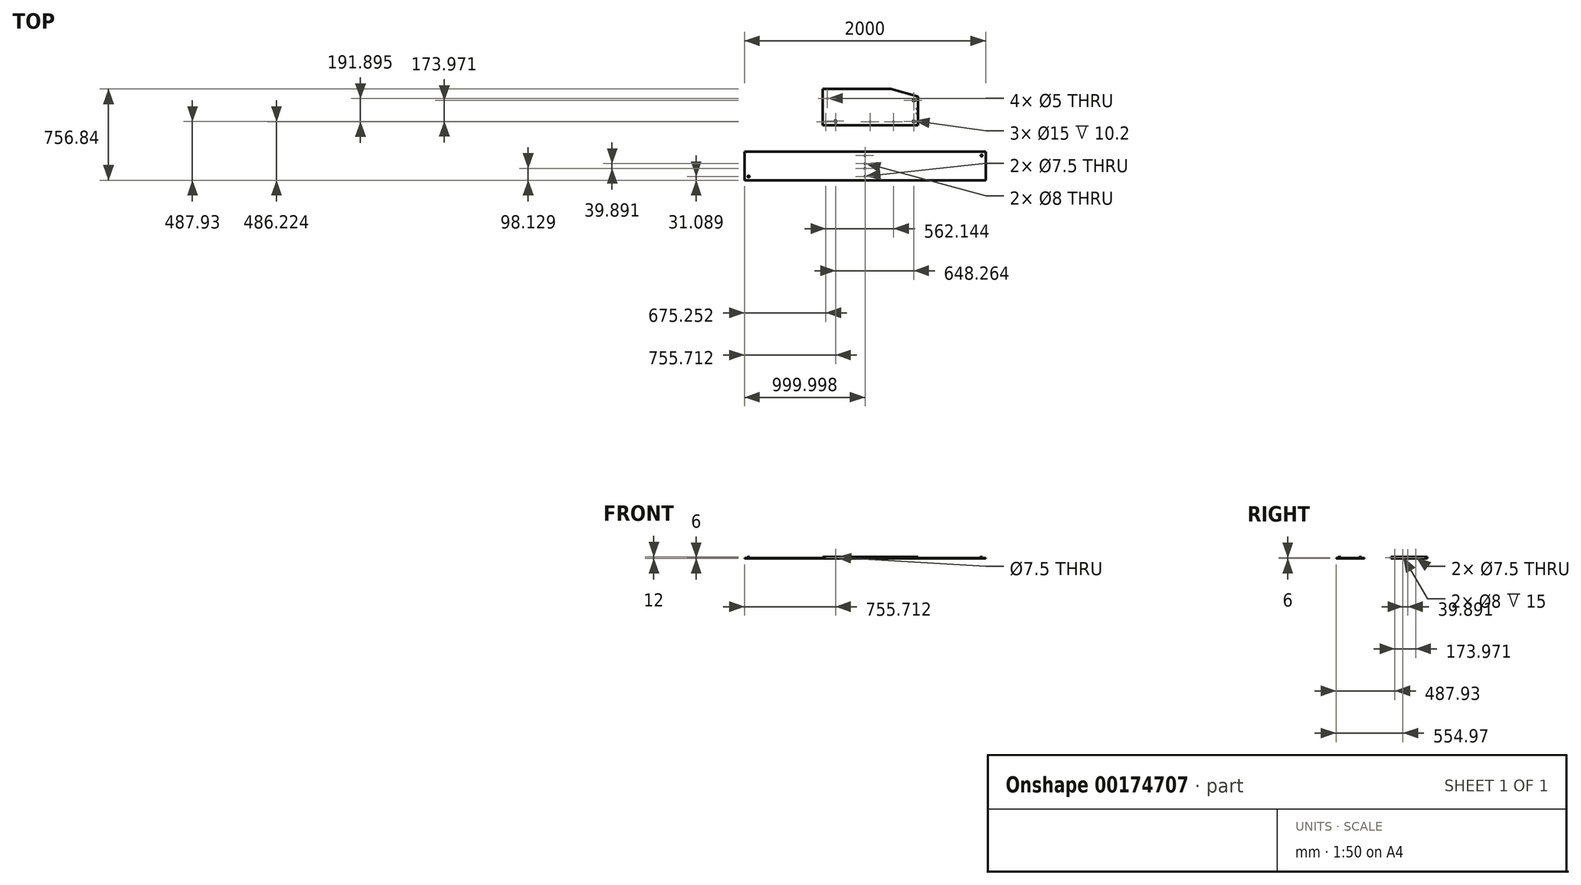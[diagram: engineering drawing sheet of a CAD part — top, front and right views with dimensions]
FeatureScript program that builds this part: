
annotation { "Feature Type Name" : "Feature", "Feature Type Description" : "" }
export const myFeature = defineFeature(function(context is Context, id is Id, definition is map)
    precondition{}
    {
        {
            var Q0;
            Q0=qCreatedBy(makeId("Top.planeOp"),FACE);
            var sketch = newSketch(context, id + "F0", { "sketchPlane" : qUnion([Q0])});
            skLineSegment(sketch, "E0.bottom", {"start": v(72.05, 333.85) * mm, "end": v(72.05, 33.85) * mm});
            skLineSegment(sketch, "E0.top", {"start": v(862.05, 270) * mm, "end": v(862.05, 33.85) * mm});
            skLineSegment(sketch, "E0.left", {"start": v(72.05, 333.85) * mm, "end": v(637.18, 333.85) * mm});
            skLineSegment(sketch, "E0.right", {"start": v(72.05, 33.85) * mm, "end": v(862.05, 33.85) * mm});
            skLineSegment(sketch, "E1", {"start": v(862.05, 270) * mm, "end": v(637.18, 333.85) * mm});
            skLineSegment(sketch, "E2.bottom", {"start": v(-575.93, -186.84) * mm, "end": v(1424.07, -186.84) * mm});
            skLineSegment(sketch, "E2.top", {"start": v(-575.93, -423) * mm, "end": v(1424.07, -423) * mm});
            skLineSegment(sketch, "E2.left", {"start": v(-575.93, -186.84) * mm, "end": v(-575.93, -423) * mm});
            skLineSegment(sketch, "E2.right", {"start": v(1424.07, -186.84) * mm, "end": v(1424.07, -423) * mm});
            skSolve(sketch);
        }
        {
            var Q0;
            Q0=makeQuery(id+"F0.imprint","IMPRINT",FACE,{"disambiguationData":[TD([[makeQuery(id+"F0.imprint","IMPRINT",EDGE,{"derivedFrom":sQuery(id+"F0.wireOp",EDGE,"E0.bottom")}),1.0]])]});
            var Q1;
            Q1=makeQuery(id+"F0.imprint","IMPRINT",FACE,{"disambiguationData":[TD([[makeQuery(id+"F0.imprint","IMPRINT",EDGE,{"derivedFrom":sQuery(id+"F0.wireOp",EDGE,"E2.bottom")}),-1.0]])]});
            extrude(context, id + "F1", {"entities" : qUnion([Q0, Q1]), "oppositeDirection" : true, "depth" : 12 * mm});
        }
        {
            var Q0;
            Q0=makeQuery(id+"F1.opExtrude","CAP_FACE",FACE,{"disambiguationData":[OSD([sQuery(id+"F0.wireOp",EDGE,"E0.bottom"),sQuery(id+"F0.wireOp",EDGE,"E0.top"),sQuery(id+"F0.wireOp",EDGE,"E0.left"),sQuery(id+"F0.wireOp",EDGE,"E0.right"),sQuery(id+"F0.wireOp",EDGE,"E1")])],"isStart":true});
            var sketch = newSketch(context, id + "F2", { "sketchPlane" : qUnion([Q0])});
            skCircle(sketch, "E3", {"center": v(828.05, 238.91) * mm, "radius": 7.5 * mm});
            skCircle(sketch, "E4", {"center": v(828.05, 64.94) * mm, "radius": 7.5 * mm});
            skCircle(sketch, "E5", {"center": v(661.47, 63.23) * mm, "radius": 2.5 * mm});
            skCircle(sketch, "E6", {"center": v(467.05, 63.23) * mm, "radius": 2.5 * mm});
            skCircle(sketch, "E7", {"center": v(99.32, 63.23) * mm, "radius": 2.5 * mm});
            skCircle(sketch, "E8", {"center": v(179.78, 67.85) * mm, "radius": 7.5 * mm});
            skCircle(sketch, "E9", {"center": v(112.37, 255.13) * mm, "radius": 2.5 * mm});
            skLineSegment(sketch, "E10", {"start": v(179.78, 67.85) * mm, "end": v(179.78, 33.85) * mm, "construction": true});
            skLineSegment(sketch, "E11", {"start": v(828.05, 64.94) * mm, "end": v(862.05, 64.94) * mm, "construction": true});
            skLineSegment(sketch, "E12", {"start": v(828.05, 238.91) * mm, "end": v(862.05, 238.91) * mm, "construction": true});
            skLineSegment(sketch, "E13", {"start": v(112.37, 255.13) * mm, "end": v(72.05, 255.13) * mm, "construction": true});
            skLineSegment(sketch, "E14", {"start": v(99.32, 63.23) * mm, "end": v(99.32, 33.85) * mm, "construction": true});
            skLineSegment(sketch, "E15", {"start": v(467.05, 63.23) * mm, "end": v(467.05, 33.85) * mm, "construction": true});
            skLineSegment(sketch, "E16", {"start": v(661.47, 63.23) * mm, "end": v(661.47, 33.85) * mm, "construction": true});
            skLineSegment(sketch, "E17", {"start": v(862.05, 151.93) * mm, "end": v(72.05, 151.93) * mm, "construction": true});
            skPoint(sketch, "E17.endSnap0", {"position": v(862.05, 151.93) * mm});
            skSolve(sketch);
        }
        {
            var Q0;
            Q0=makeQuery(id+"F1.opExtrude","SWEPT_FACE",FACE,{"disambiguationData":[OSD([sQuery(id+"F0.wireOp",EDGE,"E0.top")])]});
            var sketch = newSketch(context, id + "F3", { "sketchPlane" : qUnion([Q0])});
            skLineSegment(sketch, "E18", {"start": v(64.94, 0) * mm, "end": v(64.94, -12) * mm, "construction": true});
            skLineSegment(sketch, "E19", {"start": v(238.91, 0) * mm, "end": v(238.91, -12) * mm, "construction": true});
            skCircle(sketch, "E20", {"center": v(64.94, -6) * mm, "radius": 3.75 * mm});
            skCircle(sketch, "E21", {"center": v(238.91, -6) * mm, "radius": 3.75 * mm});
            skLineSegment(sketch, "E22", {"start": v(131.98, 0) * mm, "end": v(131.98, -12) * mm, "construction": true});
            skLineSegment(sketch, "E23", {"start": v(171.87, 0) * mm, "end": v(171.87, -12) * mm, "construction": true});
            skCircle(sketch, "E24", {"center": v(131.98, -6) * mm, "radius": 4 * mm});
            skCircle(sketch, "E25", {"center": v(171.87, -6) * mm, "radius": 4 * mm});
            skLineSegment(sketch, "E26", {"start": v(151.93, -12) * mm, "end": v(151.93, 0) * mm, "construction": true});
            skLineSegment(sketch, "E27", {"start": v(238.91, -6) * mm, "end": v(64.94, -6) * mm, "construction": true});
            skLineSegment(sketch, "E28", {"start": v(171.87, -6) * mm, "end": v(131.98, -6) * mm, "construction": true});
            skSolve(sketch);
        }
        {
            var Q0;
            Q0=makeQuery(id+"F1.opExtrude","SWEPT_FACE",FACE,{"disambiguationData":[OSD([sQuery(id+"F0.wireOp",EDGE,"E0.right")])]});
            var sketch = newSketch(context, id + "F4", { "sketchPlane" : qUnion([Q0])});
            skLineSegment(sketch, "E29", {"start": v(179.78, 0) * mm, "end": v(179.78, -12) * mm, "construction": true});
            skCircle(sketch, "E30", {"center": v(179.78, -6) * mm, "radius": 3.75 * mm});
            skSolve(sketch);
        }
        {
            var Q0;
            Q0=makeQuery(id+"F1.opExtrude","CAP_FACE",FACE,{"disambiguationData":[OSD([sQuery(id+"F0.wireOp",EDGE,"E2.bottom"),sQuery(id+"F0.wireOp",EDGE,"E2.top"),sQuery(id+"F0.wireOp",EDGE,"E2.left"),sQuery(id+"F0.wireOp",EDGE,"E2.right")])],"isStart":true});
            var sketch = newSketch(context, id + "F5", { "sketchPlane" : qUnion([Q0])});
            skLineSegment(sketch, "E31", {"start": v(424.07, -186.84) * mm, "end": v(424.07, -423) * mm, "construction": true});
            skCircle(sketch, "E32", {"center": v(424.07, -217.93) * mm, "radius": 3.75 * mm});
            skCircle(sketch, "E33", {"center": v(424.07, -391.9) * mm, "radius": 3.75 * mm});
            skCircle(sketch, "E34", {"center": v(424.07, -284.97) * mm, "radius": 4 * mm});
            skCircle(sketch, "E35", {"center": v(424.07, -324.86) * mm, "radius": 4 * mm});
            skLineSegment(sketch, "E36", {"start": v(-575.93, -304.92) * mm, "end": v(1424.07, -304.92) * mm, "construction": true});
            skPoint(sketch, "E37", {"position": v(424.07, -304.92) * mm});
            skLineSegment(sketch, "E38", {"start": v(424.07, -391.9) * mm, "end": v(424.07, -217.93) * mm, "construction": true});
            skLineSegment(sketch, "E39", {"start": v(424.07, -324.86) * mm, "end": v(424.07, -284.97) * mm, "construction": true});
            skCircle(sketch, "E40", {"center": v(-541.93, -217.93) * mm, "radius": 7.5 * mm});
            skLineSegment(sketch, "E41", {"start": v(-541.93, -217.93) * mm, "end": v(-575.93, -217.93) * mm, "construction": true});
            skCircle(sketch, "E42.MirrorC", {"center": v(-541.93, -391.9) * mm, "radius": 7.5 * mm});
            skLineSegment(sketch, "E43.MirrorCS", {"start": v(-541.93, -391.9) * mm, "end": v(-575.93, -391.9) * mm, "construction": true});
            skCircle(sketch, "E44.MirrorC", {"center": v(1390.07, -217.93) * mm, "radius": 7.5 * mm});
            skLineSegment(sketch, "E45.MirrorCS", {"start": v(1390.07, -217.93) * mm, "end": v(1424.07, -217.93) * mm, "construction": true});
            skCircle(sketch, "E46.MirrorC", {"center": v(1390.07, -391.9) * mm, "radius": 7.5 * mm});
            skLineSegment(sketch, "E47.MirrorCS", {"start": v(1390.07, -391.9) * mm, "end": v(1424.07, -391.9) * mm, "construction": true});
            skSolve(sketch);
        }
        {
            var Q0;
            Q0=makeQuery(id+"F1.opExtrude","SWEPT_FACE",FACE,{"disambiguationData":[OSD([sQuery(id+"F0.wireOp",EDGE,"E2.right")])]});
            var sketch = newSketch(context, id + "F6", { "sketchPlane" : qUnion([Q0])});
            skLineSegment(sketch, "E48", {"start": v(-391.9, 0) * mm, "end": v(-391.9, -12) * mm, "construction": true});
            skLineSegment(sketch, "E49", {"start": v(-217.93, 0) * mm, "end": v(-217.93, -12) * mm, "construction": true});
            skCircle(sketch, "E50", {"center": v(-391.9, -6) * mm, "radius": 3.75 * mm});
            skCircle(sketch, "E51", {"center": v(-217.93, -6) * mm, "radius": 3.75 * mm});
            skLineSegment(sketch, "E52", {"start": v(-324.86, 0) * mm, "end": v(-324.86, -12) * mm, "construction": true});
            skLineSegment(sketch, "E53", {"start": v(-284.97, 0) * mm, "end": v(-284.97, -12) * mm, "construction": true});
            skCircle(sketch, "E54", {"center": v(-324.86, -6) * mm, "radius": 4 * mm});
            skCircle(sketch, "E55", {"center": v(-284.97, -6) * mm, "radius": 4 * mm});
            skLineSegment(sketch, "E56", {"start": v(-304.92, -12) * mm, "end": v(-304.92, 0) * mm, "construction": true});
            skLineSegment(sketch, "E57", {"start": v(-217.93, -6) * mm, "end": v(-391.9, -6) * mm, "construction": true});
            skLineSegment(sketch, "E58", {"start": v(-284.97, -6) * mm, "end": v(-324.86, -6) * mm, "construction": true});
            skSolve(sketch);
        }
        {
            var Q0;
            Q0=makeQuery(id+"F1.opExtrude","SWEPT_FACE",FACE,{"disambiguationData":[OSD([sQuery(id+"F0.wireOp",EDGE,"E2.left")])]});
            var sketch = newSketch(context, id + "F7", { "sketchPlane" : qUnion([Q0])});
            skLineSegment(sketch, "E59", {"start": v(217.93, 0) * mm, "end": v(217.93, -12) * mm, "construction": true});
            skLineSegment(sketch, "E60", {"start": v(391.9, 0) * mm, "end": v(391.9, -12) * mm, "construction": true});
            skCircle(sketch, "E61", {"center": v(217.93, -6) * mm, "radius": 3.75 * mm});
            skCircle(sketch, "E62", {"center": v(391.9, -6) * mm, "radius": 3.75 * mm});
            skLineSegment(sketch, "E63", {"start": v(284.97, 0) * mm, "end": v(284.97, -12) * mm, "construction": true});
            skLineSegment(sketch, "E64", {"start": v(324.86, 0) * mm, "end": v(324.86, -12) * mm, "construction": true});
            skCircle(sketch, "E65", {"center": v(284.97, -6) * mm, "radius": 4 * mm});
            skCircle(sketch, "E66", {"center": v(324.86, -6) * mm, "radius": 4 * mm});
            skLineSegment(sketch, "E67", {"start": v(304.92, -12) * mm, "end": v(304.92, 0) * mm, "construction": true});
            skLineSegment(sketch, "E68", {"start": v(391.9, -6) * mm, "end": v(217.93, -6) * mm, "construction": true});
            skLineSegment(sketch, "E69", {"start": v(324.86, -6) * mm, "end": v(284.97, -6) * mm, "construction": true});
            skSolve(sketch);
        }
        {
            var Q0;
            Q0=makeQuery(id+"F2.imprint","IMPRINT",FACE,{"disambiguationData":[TD([[makeQuery(id+"F2.imprint","IMPRINT",EDGE,{"derivedFrom":sQuery(id+"F2.wireOp",EDGE,"E8")}),1.0]])]});
            var Q1;
            Q1=makeQuery(id+"F2.imprint","IMPRINT",FACE,{"disambiguationData":[TD([[makeQuery(id+"F2.imprint","IMPRINT",EDGE,{"derivedFrom":sQuery(id+"F2.wireOp",EDGE,"E4")}),1.0]])]});
            var Q2;
            Q2=makeQuery(id+"F2.imprint","IMPRINT",FACE,{"disambiguationData":[TD([[makeQuery(id+"F2.imprint","IMPRINT",EDGE,{"derivedFrom":sQuery(id+"F2.wireOp",EDGE,"E3")}),1.0]])]});
            var Q3;
            Q3=makeQuery(id+"F5.imprint","IMPRINT",FACE,{"disambiguationData":[TD([[makeQuery(id+"F5.imprint","IMPRINT",EDGE,{"derivedFrom":sQuery(id+"F5.wireOp",EDGE,"E40")}),1.0]])]});
            var Q4;
            Q4=makeQuery(id+"F5.imprint","IMPRINT",FACE,{"disambiguationData":[TD([[makeQuery(id+"F5.imprint","IMPRINT",EDGE,{"derivedFrom":sQuery(id+"F5.wireOp",EDGE,"E42.MirrorC")}),-1.0]])]});
            var Q5;
            Q5=makeQuery(id+"F5.imprint","IMPRINT",FACE,{"disambiguationData":[TD([[makeQuery(id+"F5.imprint","IMPRINT",EDGE,{"derivedFrom":sQuery(id+"F5.wireOp",EDGE,"E44.MirrorC")}),-1.0]])]});
            var Q6;
            Q6=makeQuery(id+"F5.imprint","IMPRINT",FACE,{"disambiguationData":[TD([[makeQuery(id+"F5.imprint","IMPRINT",EDGE,{"derivedFrom":sQuery(id+"F5.wireOp",EDGE,"E46.MirrorC")}),1.0]])]});
            var Q7;
            Q7=sQuery(id+"F2.wireOp",EDGE,"E8");
            var Q8;
            Q8=sQuery(id+"F2.wireOp",EDGE,"E4");
            var Q9;
            Q9=sQuery(id+"F2.wireOp",EDGE,"E3");
            extrude(context, id + "F8", {"entities" : qUnion([Q0, Q1, Q2, Q3, Q4, Q5, Q6]), "operationType" : NewBodyOperationType.REMOVE, "surfaceEntities" : qUnion([Q7, Q8, Q9]), "oppositeDirection" : true, "depth" : 10.2 * mm});
        }
        {
            var Q0;
            Q0=makeQuery(id+"F3.imprint","IMPRINT",FACE,{"disambiguationData":[TD([[makeQuery(id+"F3.imprint","IMPRINT",EDGE,{"derivedFrom":sQuery(id+"F3.wireOp",EDGE,"E20")}),1.0]])]});
            var Q1;
            Q1=makeQuery(id+"F3.imprint","IMPRINT",FACE,{"disambiguationData":[TD([[makeQuery(id+"F3.imprint","IMPRINT",EDGE,{"derivedFrom":sQuery(id+"F3.wireOp",EDGE,"E21")}),1.0]])]});
            var Q2;
            Q2=makeQuery(id+"F6.imprint","IMPRINT",FACE,{"disambiguationData":[TD([[makeQuery(id+"F6.imprint","IMPRINT",EDGE,{"derivedFrom":sQuery(id+"F6.wireOp",EDGE,"E51")}),1.0]])]});
            var Q3;
            Q3=makeQuery(id+"F6.imprint","IMPRINT",FACE,{"disambiguationData":[TD([[makeQuery(id+"F6.imprint","IMPRINT",EDGE,{"derivedFrom":sQuery(id+"F6.wireOp",EDGE,"E50")}),1.0]])]});
            var Q4;
            Q4=sQuery(id+"F3.wireOp",EDGE,"E20");
            var Q5;
            Q5=sQuery(id+"F3.wireOp",EDGE,"E21");
            extrude(context, id + "F9", {"entities" : qUnion([Q0, Q1, Q2, Q3]), "operationType" : NewBodyOperationType.REMOVE, "surfaceEntities" : qUnion([Q4, Q5]), "endBound" : BoundingType.UP_TO_NEXT, "oppositeDirection" : true, "depth" : 34 * mm});
        }
        {
            var Q0;
            Q0=makeQuery(id+"F4.imprint","IMPRINT",FACE,{"disambiguationData":[TD([[makeQuery(id+"F4.imprint","IMPRINT",EDGE,{"derivedFrom":sQuery(id+"F4.wireOp",EDGE,"E30")}),1.0]])]});
            extrude(context, id + "F10", {"entities" : qUnion([Q0]), "operationType" : NewBodyOperationType.REMOVE, "endBound" : BoundingType.UP_TO_NEXT, "oppositeDirection" : true, "depth" : 25 * mm});
        }
        {
            var Q0;
            Q0=makeQuery(id+"F2.imprint","IMPRINT",FACE,{"disambiguationData":[TD([[makeQuery(id+"F2.imprint","IMPRINT",EDGE,{"derivedFrom":sQuery(id+"F2.wireOp",EDGE,"E9")}),1.0]])]});
            var Q1;
            Q1=makeQuery(id+"F2.imprint","IMPRINT",FACE,{"disambiguationData":[TD([[makeQuery(id+"F2.imprint","IMPRINT",EDGE,{"derivedFrom":sQuery(id+"F2.wireOp",EDGE,"E7")}),1.0]])]});
            var Q2;
            Q2=makeQuery(id+"F2.imprint","IMPRINT",FACE,{"disambiguationData":[TD([[makeQuery(id+"F2.imprint","IMPRINT",EDGE,{"derivedFrom":sQuery(id+"F2.wireOp",EDGE,"E5")}),1.0]])]});
            var Q3;
            Q3=makeQuery(id+"F2.imprint","IMPRINT",FACE,{"disambiguationData":[TD([[makeQuery(id+"F2.imprint","IMPRINT",EDGE,{"derivedFrom":sQuery(id+"F2.wireOp",EDGE,"E6")}),1.0]])]});
            var Q4;
            Q4=makeQuery(id+"F5.imprint","IMPRINT",FACE,{"disambiguationData":[TD([[makeQuery(id+"F5.imprint","IMPRINT",EDGE,{"derivedFrom":sQuery(id+"F5.wireOp",EDGE,"E32")}),1.0]])]});
            var Q5;
            Q5=makeQuery(id+"F5.imprint","IMPRINT",FACE,{"disambiguationData":[TD([[makeQuery(id+"F5.imprint","IMPRINT",EDGE,{"derivedFrom":sQuery(id+"F5.wireOp",EDGE,"E34")}),1.0]])]});
            var Q6;
            Q6=makeQuery(id+"F5.imprint","IMPRINT",FACE,{"disambiguationData":[TD([[makeQuery(id+"F5.imprint","IMPRINT",EDGE,{"derivedFrom":sQuery(id+"F5.wireOp",EDGE,"E35")}),1.0]])]});
            var Q7;
            Q7=makeQuery(id+"F5.imprint","IMPRINT",FACE,{"disambiguationData":[TD([[makeQuery(id+"F5.imprint","IMPRINT",EDGE,{"derivedFrom":sQuery(id+"F5.wireOp",EDGE,"E33")}),1.0]])]});
            extrude(context, id + "F11", {"entities" : qUnion([Q0, Q1, Q2, Q3, Q4, Q5, Q6, Q7]), "operationType" : NewBodyOperationType.REMOVE, "endBound" : BoundingType.THROUGH_ALL, "oppositeDirection" : true, "depth" : 9 * mm});
        }
        {
            var Q0;
            Q0=makeQuery(id+"F3.imprint","IMPRINT",FACE,{"disambiguationData":[TD([[makeQuery(id+"F3.imprint","IMPRINT",EDGE,{"derivedFrom":sQuery(id+"F3.wireOp",EDGE,"E24")}),1.0]])]});
            var Q1;
            Q1=makeQuery(id+"F3.imprint","IMPRINT",FACE,{"disambiguationData":[TD([[makeQuery(id+"F3.imprint","IMPRINT",EDGE,{"derivedFrom":sQuery(id+"F3.wireOp",EDGE,"E25")}),1.0]])]});
            var Q2;
            Q2=makeQuery(id+"F6.imprint","IMPRINT",FACE,{"disambiguationData":[TD([[makeQuery(id+"F6.imprint","IMPRINT",EDGE,{"derivedFrom":sQuery(id+"F6.wireOp",EDGE,"E55")}),1.0]])]});
            var Q3;
            Q3=makeQuery(id+"F6.imprint","IMPRINT",FACE,{"disambiguationData":[TD([[makeQuery(id+"F6.imprint","IMPRINT",EDGE,{"derivedFrom":sQuery(id+"F6.wireOp",EDGE,"E54")}),1.0]])]});
            extrude(context, id + "F12", {"entities" : qUnion([Q0, Q1, Q2, Q3]), "operationType" : NewBodyOperationType.REMOVE, "oppositeDirection" : true, "depth" : 15 * mm});
        }
        {
            var Q0;
            Q0=makeQuery(id+"F7.imprint","IMPRINT",FACE,{"disambiguationData":[TD([[makeQuery(id+"F7.imprint","IMPRINT",EDGE,{"derivedFrom":sQuery(id+"F7.wireOp",EDGE,"E62")}),1.0]])]});
            var Q1;
            Q1=makeQuery(id+"F7.imprint","IMPRINT",FACE,{"disambiguationData":[TD([[makeQuery(id+"F7.imprint","IMPRINT",EDGE,{"derivedFrom":sQuery(id+"F7.wireOp",EDGE,"E61")}),1.0]])]});
            extrude(context, id + "F13", {"entities" : qUnion([Q0, Q1]), "operationType" : NewBodyOperationType.REMOVE, "endBound" : BoundingType.UP_TO_NEXT, "oppositeDirection" : true, "depth" : 25 * mm});
        }
        {
            var Q0;
            Q0=makeQuery(id+"F7.imprint","IMPRINT",FACE,{"disambiguationData":[TD([[makeQuery(id+"F7.imprint","IMPRINT",EDGE,{"derivedFrom":sQuery(id+"F7.wireOp",EDGE,"E65")}),1.0]])]});
            var Q1;
            Q1=makeQuery(id+"F7.imprint","IMPRINT",FACE,{"disambiguationData":[TD([[makeQuery(id+"F7.imprint","IMPRINT",EDGE,{"derivedFrom":sQuery(id+"F7.wireOp",EDGE,"E66")}),1.0]])]});
            var Q2;
            Q2=sQuery(id+"F7.wireOp",EDGE,"E66");
            var Q3;
            Q3=sQuery(id+"F7.wireOp",EDGE,"E65");
            extrude(context, id + "F14", {"entities" : qUnion([Q0, Q1]), "operationType" : NewBodyOperationType.REMOVE, "surfaceEntities" : qUnion([Q2, Q3]), "oppositeDirection" : true, "depth" : 15 * mm});
        }
    });
